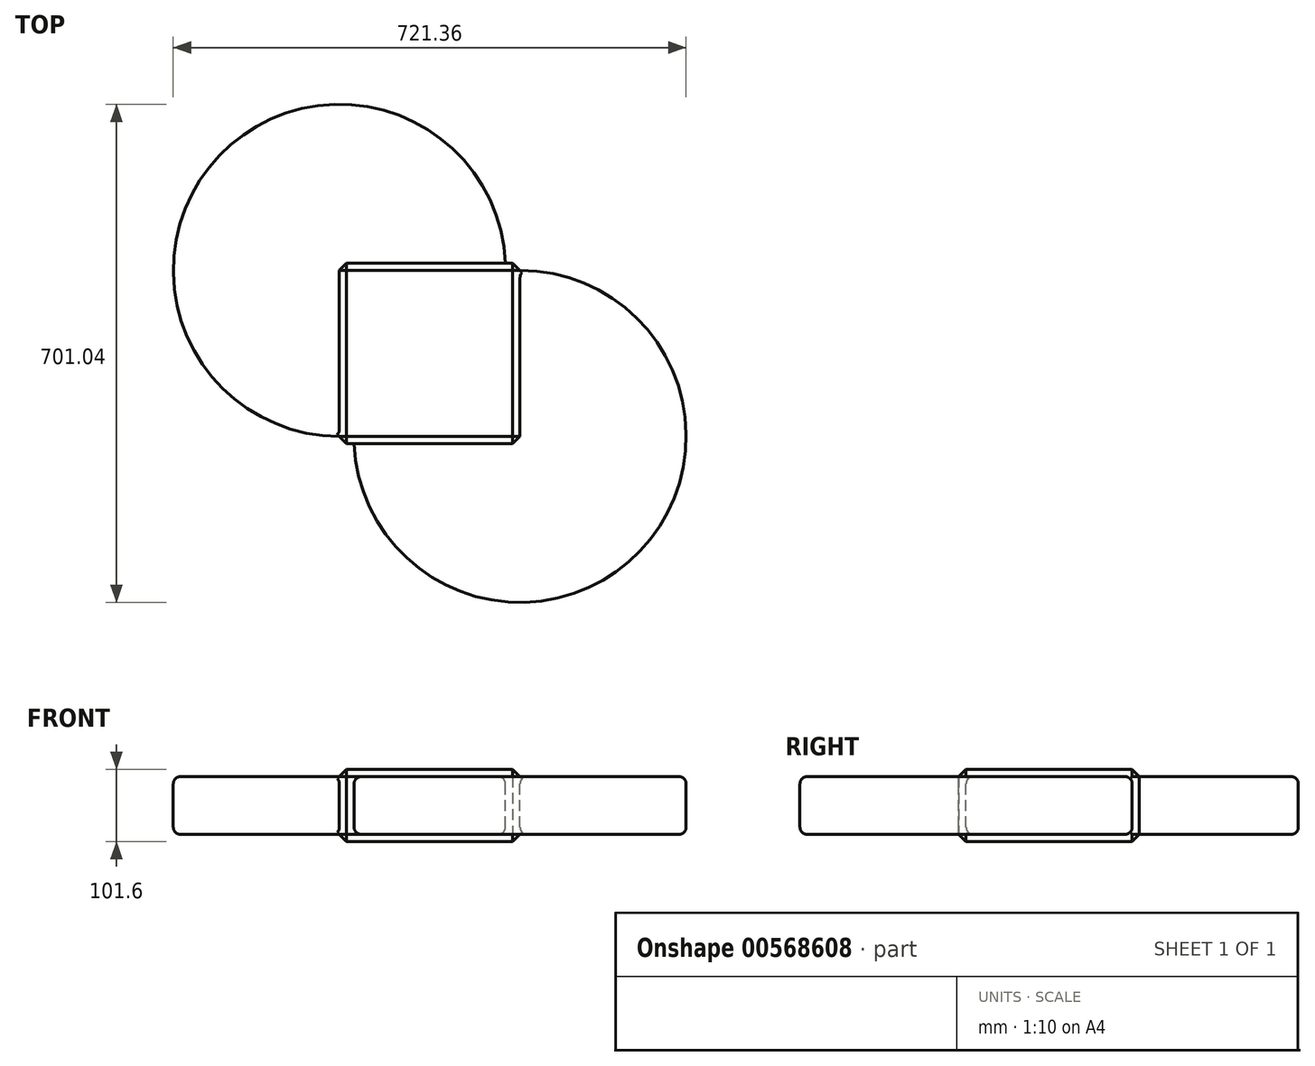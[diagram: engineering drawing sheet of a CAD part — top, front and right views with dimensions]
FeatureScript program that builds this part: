
annotation { "Feature Type Name" : "Feature", "Feature Type Description" : "" }
export const myFeature = defineFeature(function(context is Context, id is Id, definition is map)
    precondition{}
    {
        {
            var Q0;
            Q0=qCreatedBy(makeId("Top.planeOp"),FACE);
            var sketch = newSketch(context, id + "F0", { "sketchPlane" : qUnion([Q0])});
            skLineSegment(sketch, "E0.bottom", {"start": v(127, -127) * mm, "end": v(-127, -127) * mm});
            skLineSegment(sketch, "E0.top", {"start": v(127, 127) * mm, "end": v(-127, 127) * mm});
            skLineSegment(sketch, "E0.left", {"start": v(127, -127) * mm, "end": v(127, 127) * mm});
            skLineSegment(sketch, "E0.right", {"start": v(-127, -127) * mm, "end": v(-127, 127) * mm});
            skPoint(sketch, "E0.middle", {"position": v(0, 0) * mm});
            skSolve(sketch);
        }
        {
            var Q0;
            Q0=makeQuery(id+"F0.imprint","IMPRINT",FACE,{"disambiguationData":[TD([[makeQuery(id+"F0.imprint","IMPRINT",EDGE,{"derivedFrom":sQuery(id+"F0.wireOp",EDGE,"E0.bottom")}),-1.0]])]});
            extrude(context, id + "F1", {"entities" : qUnion([Q0]), "depth" : 50.8 * mm, "offsetDistance" : 25.4 * mm, "hasSecondDirection" : true, "secondDirectionOppositeDirection" : true, "secondDirectionDepth" : 50.8 * mm});
        }
        {
            var Q0;
            Q0=makeQuery(id+"F1.opExtrude","CAP_EDGE",EDGE,{"disambiguationData":[OSD([sQuery(id+"F0.wireOp",EDGE,"E0.bottom")])],"isStart":false});
            var Q1;
            Q1=makeQuery(id+"F1.opExtrude","SWEPT_EDGE",EDGE,{"disambiguationData":[OSD([sQuery(id+"F0.wireOp",EDGE,"E0.bottom"),sQuery(id+"F0.wireOp",EDGE,"E0.left")])]});
            var Q2;
            Q2=makeQuery(id+"F1.opExtrude","CAP_EDGE",EDGE,{"disambiguationData":[OSD([sQuery(id+"F0.wireOp",EDGE,"E0.left")])],"isStart":false});
            var Q3;
            Q3=makeQuery(id+"F1.opExtrude","SWEPT_EDGE",EDGE,{"disambiguationData":[OSD([sQuery(id+"F0.wireOp",EDGE,"E0.bottom"),sQuery(id+"F0.wireOp",EDGE,"E0.right")])]});
            var Q4;
            Q4=makeQuery(id+"F1.opExtrude","CAP_EDGE",EDGE,{"disambiguationData":[OSD([sQuery(id+"F0.wireOp",EDGE,"E0.bottom")])],"isStart":true});
            var Q5;
            Q5=makeQuery(id+"F1.opExtrude","CAP_EDGE",EDGE,{"disambiguationData":[OSD([sQuery(id+"F0.wireOp",EDGE,"E0.left")])],"isStart":true});
            var Q6;
            Q6=makeQuery(id+"F1.opExtrude","SWEPT_EDGE",EDGE,{"disambiguationData":[OSD([sQuery(id+"F0.wireOp",EDGE,"E0.top"),sQuery(id+"F0.wireOp",EDGE,"E0.left")])]});
            var Q7;
            Q7=makeQuery(id+"F1.opExtrude","CAP_EDGE",EDGE,{"disambiguationData":[OSD([sQuery(id+"F0.wireOp",EDGE,"E0.right")])],"isStart":false});
            var Q8;
            Q8=makeQuery(id+"F1.opExtrude","CAP_EDGE",EDGE,{"disambiguationData":[OSD([sQuery(id+"F0.wireOp",EDGE,"E0.right")])],"isStart":true});
            var Q9;
            Q9=makeQuery(id+"F1.opExtrude","SWEPT_EDGE",EDGE,{"disambiguationData":[OSD([sQuery(id+"F0.wireOp",EDGE,"E0.top"),sQuery(id+"F0.wireOp",EDGE,"E0.right")])]});
            var Q10;
            Q10=makeQuery(id+"F1.opExtrude","CAP_EDGE",EDGE,{"disambiguationData":[OSD([sQuery(id+"F0.wireOp",EDGE,"E0.top")])],"isStart":false});
            var Q11;
            Q11=makeQuery(id+"F1.opExtrude","CAP_EDGE",EDGE,{"disambiguationData":[OSD([sQuery(id+"F0.wireOp",EDGE,"E0.top")])],"isStart":true});
            chamfer(context, id + "F2", {"entities" : qUnion([Q0, Q1, Q2, Q3, Q4, Q5, Q6, Q7, Q8, Q9, Q10, Q11]), "width" : 10.16 * mm, "tangentPropagation" : true});
        }
        {
            var Q0;
            Q0=makeQuery(id+"F1.opExtrude","SWEPT_FACE",FACE,{"disambiguationData":[OSD([sQuery(id+"F0.wireOp",EDGE,"E0.left")])]});
            var Q1;
            {var subQ0=sQuery(id+"F0.wireOp",EDGE,"E0.left");Q1=makeQuery(id+"F2.opChamfer","BLEND_EDGE",EDGE,{"blendedFrom":[makeQuery(id+"F1.opExtrude","SWEPT_EDGE",EDGE,{"disambiguationData":[OSD([sQuery(id+"F0.wireOp",EDGE,"E0.bottom"),subQ0])]}),makeQuery(id+"F1.opExtrude","SWEPT_FACE",FACE,{"disambiguationData":[OSD([subQ0])]})],"blendedInto":[makeQuery(id+"F1.opExtrude","SWEPT_FACE",FACE,{"disambiguationData":[OSD([subQ0])]})]});}
            revolve(context, id + "F3", {"operationType" : NewBodyOperationType.ADD, "entities" : qUnion([Q0]), "axis" : qUnion([Q1]), "revolveType" : RevolveType.FULL});
        }
        {
            var Q0;
            Q0=makeQuery(id+"F1.opExtrude","SWEPT_FACE",FACE,{"disambiguationData":[OSD([sQuery(id+"F0.wireOp",EDGE,"E0.right")])]});
            var Q1;
            {var subQ0=sQuery(id+"F0.wireOp",EDGE,"E0.right");Q1=makeQuery(id+"F2.opChamfer","BLEND_EDGE",EDGE,{"blendedFrom":[makeQuery(id+"F1.opExtrude","SWEPT_EDGE",EDGE,{"disambiguationData":[OSD([sQuery(id+"F0.wireOp",EDGE,"E0.top"),subQ0])]}),makeQuery(id+"F1.opExtrude","SWEPT_FACE",FACE,{"disambiguationData":[OSD([subQ0])]})],"blendedInto":[makeQuery(id+"F1.opExtrude","SWEPT_FACE",FACE,{"disambiguationData":[OSD([subQ0])]})]});}
            revolve(context, id + "F4", {"operationType" : NewBodyOperationType.ADD, "entities" : qUnion([Q0]), "axis" : qUnion([Q1]), "revolveType" : RevolveType.FULL});
        }
        {
            var Q0;
            {var subQ0=sQuery(id+"F0.wireOp",EDGE,"E0.left");var subQ1=sQuery(id+"F0.wireOp",EDGE,"E0.top");Q0=makeQuery(id+"F3.opRevolve","SWEPT_EDGE",EDGE,{"disambiguationData":[OSD([subQ1,subQ0]),TDD([makeQuery(id+"F2.opChamfer","BLEND_VERTEX",VERTEX,{"blendedFrom":[makeQuery(id+"F1.opExtrude","CAP_VERTEX",VERTEX,{"disambiguationData":[OSD([subQ1,subQ0])],"isStart":false}),makeQuery(id+"F1.opExtrude","SWEPT_EDGE",EDGE,{"disambiguationData":[OSD([subQ1,subQ0])]}),makeQuery(id+"F1.opExtrude","CAP_EDGE",EDGE,{"disambiguationData":[OSD([subQ0])],"isStart":false}),makeQuery(id+"F1.opExtrude","SWEPT_FACE",FACE,{"disambiguationData":[OSD([subQ0])]})],"blendedInto":[makeQuery(id+"F1.opExtrude","SWEPT_FACE",FACE,{"disambiguationData":[OSD([subQ0])]})]})])]});}
            var Q1;
            {var subQ0=sQuery(id+"F0.wireOp",EDGE,"E0.left");var subQ1=sQuery(id+"F0.wireOp",EDGE,"E0.top");Q1=makeQuery(id+"F3.opRevolve","SWEPT_EDGE",EDGE,{"disambiguationData":[OSD([subQ1,subQ0]),TDD([makeQuery(id+"F2.opChamfer","BLEND_VERTEX",VERTEX,{"blendedFrom":[makeQuery(id+"F1.opExtrude","CAP_VERTEX",VERTEX,{"disambiguationData":[OSD([subQ1,subQ0])],"isStart":true}),makeQuery(id+"F1.opExtrude","SWEPT_EDGE",EDGE,{"disambiguationData":[OSD([subQ1,subQ0])]}),makeQuery(id+"F1.opExtrude","CAP_EDGE",EDGE,{"disambiguationData":[OSD([subQ0])],"isStart":true}),makeQuery(id+"F1.opExtrude","SWEPT_FACE",FACE,{"disambiguationData":[OSD([subQ0])]})],"blendedInto":[makeQuery(id+"F1.opExtrude","SWEPT_FACE",FACE,{"disambiguationData":[OSD([subQ0])]})]})])]});}
            var Q2;
            {var subQ0=sQuery(id+"F0.wireOp",EDGE,"E0.right");var subQ1=sQuery(id+"F0.wireOp",EDGE,"E0.bottom");Q2=makeQuery(id+"F4.opRevolve","SWEPT_EDGE",EDGE,{"disambiguationData":[OSD([subQ1,subQ0]),TDD([makeQuery(id+"F2.opChamfer","BLEND_VERTEX",VERTEX,{"blendedFrom":[makeQuery(id+"F1.opExtrude","CAP_VERTEX",VERTEX,{"disambiguationData":[OSD([subQ1,subQ0])],"isStart":false}),makeQuery(id+"F1.opExtrude","SWEPT_EDGE",EDGE,{"disambiguationData":[OSD([subQ1,subQ0])]}),makeQuery(id+"F1.opExtrude","CAP_EDGE",EDGE,{"disambiguationData":[OSD([subQ0])],"isStart":false}),makeQuery(id+"F1.opExtrude","SWEPT_FACE",FACE,{"disambiguationData":[OSD([subQ0])]})],"blendedInto":[makeQuery(id+"F1.opExtrude","SWEPT_FACE",FACE,{"disambiguationData":[OSD([subQ0])]})]})])]});}
            var Q3;
            {var subQ0=sQuery(id+"F0.wireOp",EDGE,"E0.right");var subQ1=sQuery(id+"F0.wireOp",EDGE,"E0.bottom");Q3=makeQuery(id+"F4.opRevolve","SWEPT_EDGE",EDGE,{"disambiguationData":[OSD([subQ1,subQ0]),TDD([makeQuery(id+"F2.opChamfer","BLEND_VERTEX",VERTEX,{"blendedFrom":[makeQuery(id+"F1.opExtrude","CAP_VERTEX",VERTEX,{"disambiguationData":[OSD([subQ1,subQ0])],"isStart":true}),makeQuery(id+"F1.opExtrude","SWEPT_EDGE",EDGE,{"disambiguationData":[OSD([subQ1,subQ0])]}),makeQuery(id+"F1.opExtrude","CAP_EDGE",EDGE,{"disambiguationData":[OSD([subQ0])],"isStart":true}),makeQuery(id+"F1.opExtrude","SWEPT_FACE",FACE,{"disambiguationData":[OSD([subQ0])]})],"blendedInto":[makeQuery(id+"F1.opExtrude","SWEPT_FACE",FACE,{"disambiguationData":[OSD([subQ0])]})]})])]});}
            fillet(context, id + "F5", {"entities" : qUnion([Q0, Q1, Q2, Q3]), "radius" : 10.16 * mm, "tangentPropagation" : true, "allowEdgeOverflow" : false});
        }
    });
